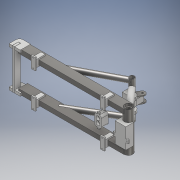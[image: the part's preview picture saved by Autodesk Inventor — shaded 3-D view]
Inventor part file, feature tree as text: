
AUTODESK INVENTOR PART (.ipt)
format: ipt  version: 2019.2 (Build 232265000, 265)  size: 610,816 bytes
history: native  units: mm
features: other x17, plane x1, extrude x1, sketch x1
ambient origin geometry x8: Origin, YZ Plane, XZ Plane, XY Plane, X Axis, Y Axis, Z Axis, Center Point
bodies: Solid1 (feature_tree), Solid3 (feature_tree), Solid13 (feature_tree), Solid14 (feature_tree), Solid15 (feature_tree), Solid20 (feature_tree), Solid21 (feature_tree), Solid22 (feature_tree), Solid23 (feature_tree), Solid24 (feature_tree)
feature tree (20):
  other  "Swingarm.ipt"
  other  "Swingarm2.ipt"
  other  "Jig.ipt"
  plane  "Work Plane2"
  extrude  "Extrusion20"  [1 undecoded]
  other  "Arms::Swingarm.ipt"
  other  "ShockPlate::Swingarm.ipt"
  other  "TaggingFeature1"
  sketch  "Sketch21"  dims[d0=10.0mm d14=-235.5mm d60=180.0mm d61=0.0mm d70=10.0mm d92=10.0mm]
  other  "Dropout::Swingarm2.ipt"
  other  "Solid5::Swingarm2.ipt"
  other  "TaggingFeature2"
  other  "Solid6::Swingarm2.ipt"
  other  "DropoutAlign"
  other  "PivotCup::Swingarm.ipt"
  other  "JigPartA::Jig.ipt"
  other  "JigPartB-up::Jig.ipt"
  other  "JigPartB-bottom::Jig.ipt"
  other  "JigPartC::Jig.ipt"
  other  "TaggingFeature3"
note: 1 required parameter value undecoded (feature->parameter linkage not recoverable at this tier; creation-order binding heuristic only, values carry confidence <= 0.55)
